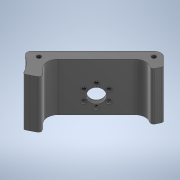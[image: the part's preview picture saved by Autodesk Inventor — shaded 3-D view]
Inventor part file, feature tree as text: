
AUTODESK INVENTOR PART (.ipt)
format: ipt  version: 2020 (Build 240168000, 168)  size: 390,656 bytes
history: native  units: mm
features: extrude x4, sketch x3, other x1, chamfer x1, fillet x1
ambient origin geometry x8: Origin, YZ Plane, XZ Plane, XY Plane, X Axis, Y Axis, Z Axis, Center Point
bodies: Body1 (feature_tree)
feature tree (10):
  other  "Твердое тело1"
  sketch  "Эскиз1"
  extrude  "Выдавливание10"  Depth=3.0mm
  sketch  "Эскиз6"
  extrude  "Выдавливание13"  Depth=6.0mm
  extrude  "Выдавливание14"  Depth=35.0mm TaperAngle=0.0deg
  chamfer  "Фаска3"  Distance=59.0mm
  extrude  "Выдавливание15"  Depth=21.3mm
  fillet  "Сопряжение1"  Radius=15.0mm
  sketch  "Эскиз7"
